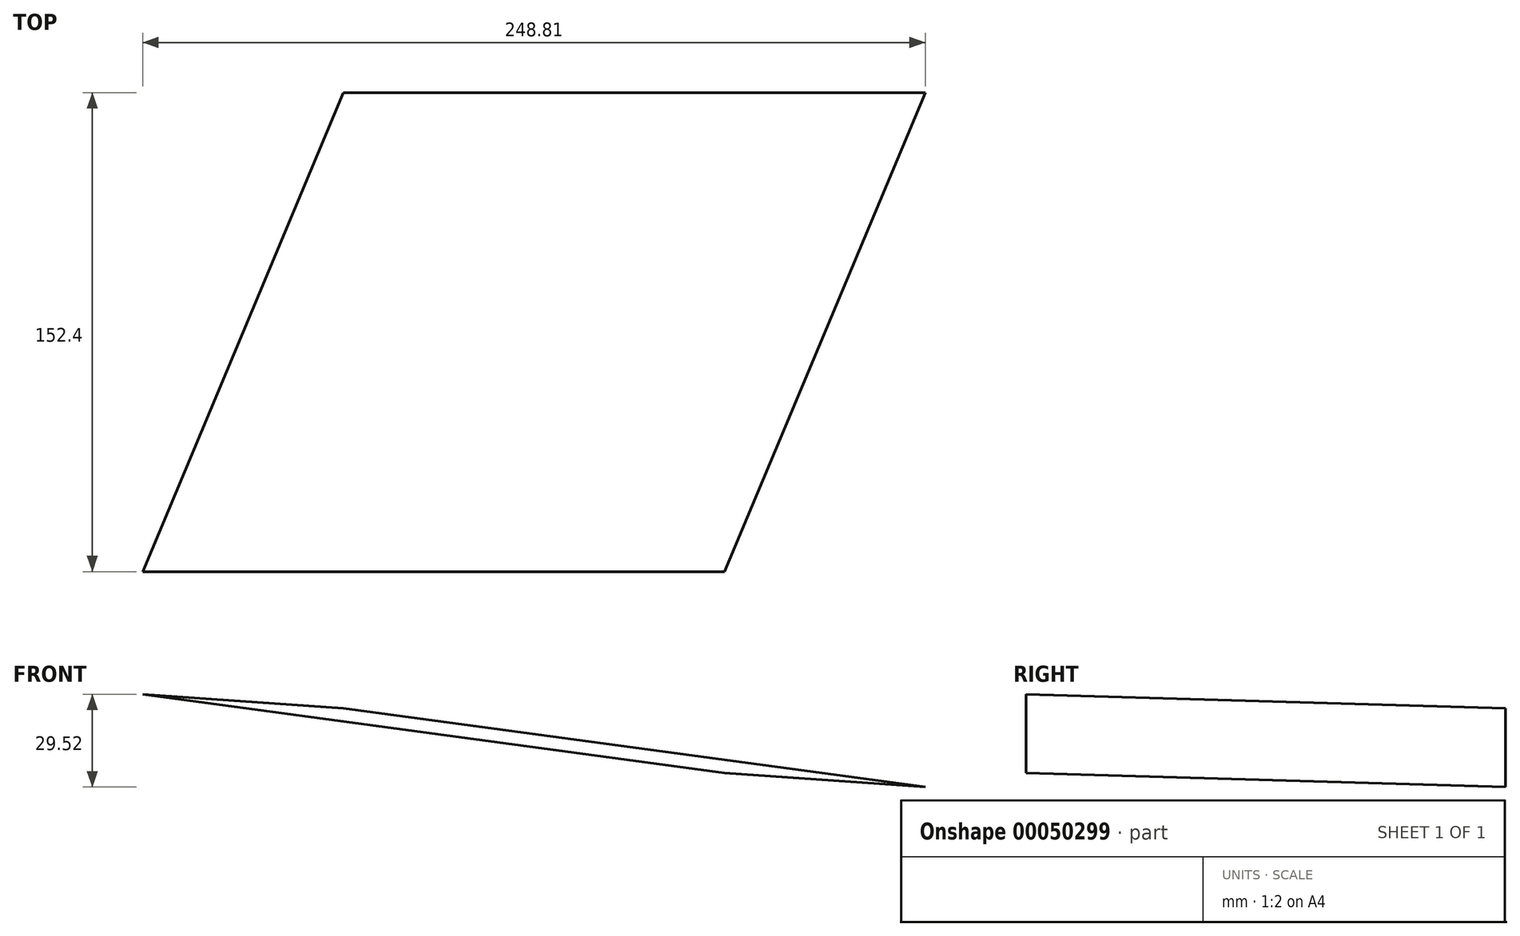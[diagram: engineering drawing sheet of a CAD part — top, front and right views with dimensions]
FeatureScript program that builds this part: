
annotation { "Feature Type Name" : "Feature", "Feature Type Description" : "" }
export const myFeature = defineFeature(function(context is Context, id is Id, definition is map)
    precondition{}
    {
        {
            var Q0;
            Q0=qCreatedBy(makeId("Front.planeOp"),FACE);
            var sketch = newSketch(context, id + "F0", { "sketchPlane" : qUnion([Q0])});
            skLineSegment(sketch, "E0", {"start": v(-71.25, 0) * mm, "end": v(68.24, 0) * mm, "construction": true});
            skArc(sketch, "E1", {"start": v(0, 25.4) * mm, "mid": v(-25.4, 0) * mm, "end": v(0, -25.4) * mm});
            skArc(sketch, "E2", {"start": v(184.96, -50.46) * mm, "mid": v(228.09, -15.26) * mm, "end": v(190.08, 25.4) * mm});
            skLineSegment(sketch, "E3", {"start": v(0, 25.4) * mm, "end": v(190.08, 25.4) * mm});
            skLineSegment(sketch, "E4", {"start": v(0, -25.4) * mm, "end": v(184.96, -50.46) * mm});
            skSolve(sketch);
        }
        {
            var Q0;
            Q0=qCreatedBy(makeId("Front.planeOp"),FACE);
            cPlane(context, id + "F1", {"entities" : qUnion([Q0]), "cplaneType" : CPlaneType.OFFSET, "offset" : 152.4 * mm, "width" : 152.4 * mm, "height" : 152.4 * mm});
        }
        {
            var Q0;
            Q0=qCreatedBy(id+"F1.planeOp",FACE);
            var sketch = newSketch(context, id + "F2", { "sketchPlane" : qUnion([Q0])});
            skLineSegment(sketch, "E5", {"start": v(-135.1, 4.46) * mm, "end": v(4.4, 4.46) * mm, "construction": true});
            skArc(sketch, "E6", {"start": v(-63.85, 29.86) * mm, "mid": v(-89.25, 4.46) * mm, "end": v(-63.85, -20.94) * mm});
            skArc(sketch, "E7", {"start": v(121.12, -46) * mm, "mid": v(164.24, -10.8) * mm, "end": v(126.23, 29.86) * mm});
            skLineSegment(sketch, "E8", {"start": v(-63.85, 29.86) * mm, "end": v(126.23, 29.86) * mm});
            skLineSegment(sketch, "E9", {"start": v(-63.85, -20.94) * mm, "end": v(121.12, -46) * mm});
            skSolve(sketch);
        }
        {
            var Q0;
            Q0=sQuery(id+"F2.wireOp",EDGE,"E9");
            var Q1;
            Q1=sQuery(id+"F0.wireOp",EDGE,"E4");
            loft(context, id + "F3", {"bodyType" : ToolBodyType.SURFACE, "wireProfilesArray" : [{ "wireProfileEntities" : qUnion([Q0]) }, { "wireProfileEntities" : qUnion([Q1]) }]});
        }
    });
